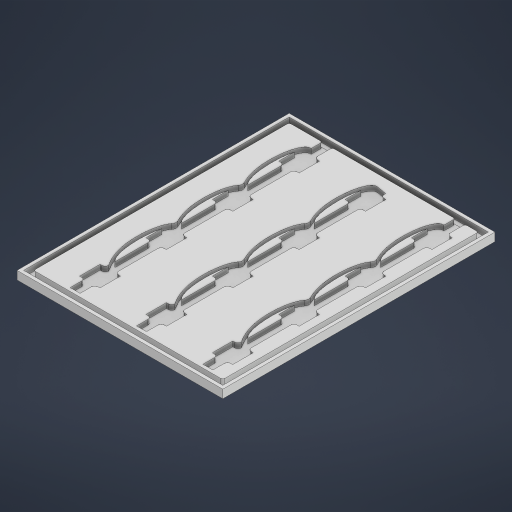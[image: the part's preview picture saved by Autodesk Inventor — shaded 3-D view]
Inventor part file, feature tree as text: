
AUTODESK INVENTOR PART (.ipt)
format: ipt  version: 2023 (Build 270158030, 158C)  size: 1,371,648 bytes
history: native  units: mm
features: sketch x7, extrude x6, delete_face x5, fillet x3, direct_edit x3, pattern_linear x2, other x2, projected_geometry x2, move_body x2, chamfer x1
ambient origin geometry x8: Origin, YZ Plane, XZ Plane, XY Plane, X Axis, Y Axis, Z Axis, Center Point
bodies: Volumenkörper1 (feature_tree)
feature tree (33):
  extrude  "Extrusion1"  Depth=12.3mm
  extrude  "Extrusion2"  Depth=120.0mm
  extrude  "Extrusion3"  Depth=3.0mm TaperAngle=0.0deg
  chamfer  "Fase1"  Distance=2.0mm
  fillet  "Rundung1"  Radius=6.0mm
  pattern_linear  "Rechteckige Anordnung2"  Count1=3  [1 undecoded]
  extrude  "Extrusion5"  Depth=1.25mm
  direct_edit  "Direktbearbeitung1"
  sketch  "Sketch12"  dims[d18=10.0mm d19=0.0mm]
  extrude  "Extrusion11"  Depth=1.25mm
  delete_face  "Delete Face1"
  pattern_linear  "Rectangular Pattern4"  Spacing1=2.0mm  [1 undecoded]
  delete_face  "Delete Face2"
  fillet  "Fillet3"  Radius=3.5mm
  delete_face  "Delete Face3"
  delete_face  "Delete Face4"
  extrude  "Extrusion16"  Depth=1.25mm TaperAngle=0.0deg
  direct_edit  "Direct Edit3"
  delete_face  "Delete Face5"
  direct_edit  "Direct Edit4"
  fillet  "Fillet7"  Radius=3.5mm
  sketch  "Skizze1"  dims[d0=12.3mm d1=12.3mm]
  sketch  "Skizze2"  dims[d2=30.0mm d4=40.0mm d5=40.0mm d7=40.0mm d10=120.0mm]
  sketch  "Skizze3"  dims[d11=160.0mm d12=3.0mm d13=0.0mm d14=2.0mm d15=0.0mm d16=6.0mm]
  sketch  "Skizze5"  dims[d17=27.0mm]
  other  "Image2"
  sketch  "Sketch13"  dims[d20=1.5mm d21=2.0mm d22=45.0deg]
  projected_geometry  "Projected Loop1"
  sketch  "Sketch18"  dims[d29=2.0mm d30=30.0mm d32=40.0mm d33=40.0mm d35=40.0mm d49=3.0mm d50=2.0mm d51=3.5mm d52=0.0mm d53=8.5mm d54=0.0mm d55=0.0mm d124=3.5mm d125=0.0mm d126=30.0mm d128=40.0mm d129=30.0mm d131=40.0mm d139=3.0mm d162=2.0mm d163=10.0mm d164=0.0mm d165=-1.0mm d175=-2.5mm d176=0.0mm d177=0.0mm d181=1.25mm]
  projected_geometry  "Projected Loop2"
  move_body  "Verschieben1"
  other  "Size1"
  move_body  "Move3"
note: 2 required parameter values undecoded (feature->parameter linkage not recoverable at this tier; creation-order binding heuristic only, values carry confidence <= 0.55)
